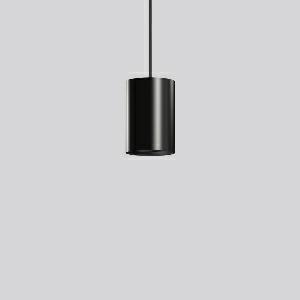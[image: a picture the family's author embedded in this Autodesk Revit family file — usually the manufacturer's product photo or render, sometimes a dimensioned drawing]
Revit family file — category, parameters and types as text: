
# Revit family: deecos_p_maxi_911551_003_e9e9
name_source: partatom
category: Lighting Fixtures
units: mm (PartAtom-declared; Revit-internal decimal feet)

## family parameters
Cut with Voids When Loaded = No
Host = Face
Light Source = No
Part Type = Normal
Room Calculation Point = No
Round Connector Dimension = Use Diameter
Shared = No

## types (1)
- DEECOS P maxi (1 x LED Modul 920 meat+, 2250 lm, 2000)
    Apparent Load = 33 VA
    Approval mark = CE
    CIE Flux Codes = 100 100 100 100 100
    Color Rendering = 90
    Color Temperature = 2000
    Default Elevation = 1800 mm
    Description = Series: DEECOS P maxi
Cylindrical pendant luminaire. Housing: die-cast aluminium, powder-coated. Canopy made of powder-coated sheet steel with magnetic attachment. Optical assembly with reflector made of MIRO-Silver with 98% total light reflection for outstanding efficiency - can be changed without tools. Including special LED for illuminating meat products / Meat plus - intense red. Transparent suspension cable 2 m, can be shortened. High quality converter without flickering and stroboscopic effect. The following accessories can be mounted without use of tools: interchangeable lenses, honeycomb louvre, clear and frosted diffusers, white interchangeable plastic ring. Decorative recessed suspension set available as accessory. 
Colour: deep black, matt (RAL 9005)
Diameter: 123 mm
Height: 181 mm
Suspension length: 2000 mm
Lamp: LED
Socket: without socket
Colour temperature: meat +
Colour rendering index (CRI): 92
System power: 33 W
Rated luminous flux: 2250 lm
Luminous efficiency: 68 lm/W
Control gear: Regulated power supply
Protection class: I
Type of protection: IP 20
    Height = 181 mm
    Lamp = 1 x LED Modul 920 meat+
    Lamp Light Flux = 2250 lm
    Lamp count = 1
    Length = 123 mm
    Lifetime = 50000 h
    Luminous efficacy = 68 lm/W
    Manufacturer = RZB
    ModVariant = No
    Model = 911551.003
    Mounting Place = Ceiling
    Mounting Type = Pendant
    Number of Poles = 1
    OnlyDefault = Yes
    Power Factor = 1
    Product Name = DEECOS P maxi
    Product group = Pendant luminaires
    ProductGroupID = 902
    Protection Class = Protection class I
    Protection Degree = IP 20
    RLX_Detail_Level = 1
    RLX_Emergency_Light_Flux = 0 lm
    RLX_Emergency_Type = 0
    RLX_Emergency_Type_DB = No
    RlxData = <blob elided: 36689 chars, md5=ab5147e6>
    Socket = socket
    Standby Power = 0 W
    System Light Flux = 2250 lm
    System Power = 33 W
    Type Comments = Product without accessories
    Type Image = 911480.003.jpg
    URL = http://relux.com
    VarID = ---
    Voltage = 230 V
    Voltage Range = 220-240 V
    Weight = 0.00 kg
    Width = 0 mm  [stored 0 ft]

note: [stored X ft] marks values corroborated as IEEE doubles in the binary element streams (Revit-internal decimal feet)

## geometry (parser evidence)
native form markers: Blend x4, Sweep x10
no freeform markers — native parametric forms only
